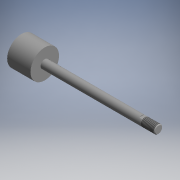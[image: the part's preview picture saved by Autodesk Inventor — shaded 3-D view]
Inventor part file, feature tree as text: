
AUTODESK INVENTOR PART (.ipt)
format: ipt  version: 2017.3 (Build 213256000, 256)  size: 161,280 bytes
history: native  units: mm (DEFAULTED — no unit token found)
features: other x98, sketch x3, revolve x2, thread x1, extrude x1
ambient origin geometry x8: Origin, YZ Plane, XZ Plane, XY Plane, X Axis, Y Axis, Z Axis, Center Point
bodies: Solid1 (feature_tree)
feature tree (105):
  revolve  "Revolution1"  Angle=360.0deg
  revolve  "Revolution2"  [1 undecoded]
  thread  "Thread1"  [1 undecoded]
  extrude  "Extrusion1"  [1 undecoded]
  other  "dia1_XY"
  other  "dia1_YZ"
  other  "dia1_ZX"
  other  "dia1_X"
  other  "dia1_Y"
  other  "dia1_Z"
  other  "dia1_Center"
  other  "dia12_XY"
  other  "dia12_YZ"
  other  "dia12_ZX"
  other  "dia12_X"
  other  "dia12_Y"
  other  "dia12_Z"
  other  "dia12_Center"
  other  "dia2_XY"
  other  "dia2_YZ"
  other  "dia2_ZX"
  other  "dia2_X"
  other  "dia2_Y"
  other  "dia2_Z"
  other  "dia2_Center"
  other  "dia22_XY"
  other  "dia22_YZ"
  other  "dia22_ZX"
  other  "dia22_X"
  other  "dia22_Y"
  other  "dia22_Z"
  other  "dia22_Center"
  other  "rl1_XY"
  other  "rl1_YZ"
  other  "rl1_ZX"
  other  "rl1_X"
  other  "rl1_Y"
  other  "rl1_Z"
  other  "rl1_Center"
  other  "rl2_XY"
  other  "rl2_YZ"
  other  "rl2_ZX"
  other  "rl2_X"
  other  "rl2_Y"
  other  "rl2_Z"
  other  "rl2_Center"
  other  "rod_cp_XY"
  other  "rod_cp_YZ"
  other  "rod_cp_ZX"
  other  "rod_cp_X"
  other  "rod_cp_Y"
  other  "rod_cp_Z"
  other  "rod_cp_Center"
  other  "thd1_XY"
  other  "thd1_YZ"
  other  "thd1_ZX"
  other  "thd1_X"
  other  "thd1_Y"
  other  "thd1_Z"
  other  "thd1_Center"
  other  "thd2_XY"
  other  "thd2_YZ"
  other  "thd2_ZX"
  other  "thd2_X"
  other  "thd2_Y"
  other  "thd2_Z"
  other  "thd2_Center"
  other  "to_rod_clevis_XY"
  other  "to_rod_clevis_YZ"
  other  "to_rod_clevis_ZX"
  other  "to_rod_clevis_X"
  other  "to_rod_clevis_Y"
  other  "to_rod_clevis_Z"
  other  "to_rod_clevis_Center"
  other  "wf1_XY"
  other  "wf1_YZ"
  other  "wf1_ZX"
  other  "wf1_X"
  other  "wf1_Y"
  other  "wf1_Z"
  other  "wf1_Center"
  other  "wf2_XY"
  other  "wf2_YZ"
  other  "wf2_ZX"
  other  "wf2_X"
  other  "wf2_Y"
  other  "wf2_Z"
  other  "wf2_Center"
  other  "wfw1_XY"
  other  "wfw1_YZ"
  other  "wfw1_ZX"
  other  "wfw1_X"
  other  "wfw1_Y"
  other  "wfw1_Z"
  other  "wfw1_Center"
  other  "wfw2_XY"
  other  "wfw2_YZ"
  other  "wfw2_ZX"
  other  "wfw2_X"
  other  "wfw2_Y"
  other  "wfw2_Z"
  other  "wfw2_Center"
  sketch  "Sketch_1"  dims[d0=360.0deg d1=360.0deg]
  sketch  "Sketch_3"  dims[d2=12.0701mm d3=0.0mm d4=3.175mm d5=0.0mm]
  sketch  "Sketch_10"  dims[d6=0.0mm d7=0.0mm d8=0.0mm d9=0.0mm d10=0.0mm d11=0.0mm d12=0.0mm]
note: 3 required parameter values undecoded (feature->parameter linkage not recoverable at this tier; creation-order binding heuristic only, values carry confidence <= 0.55)